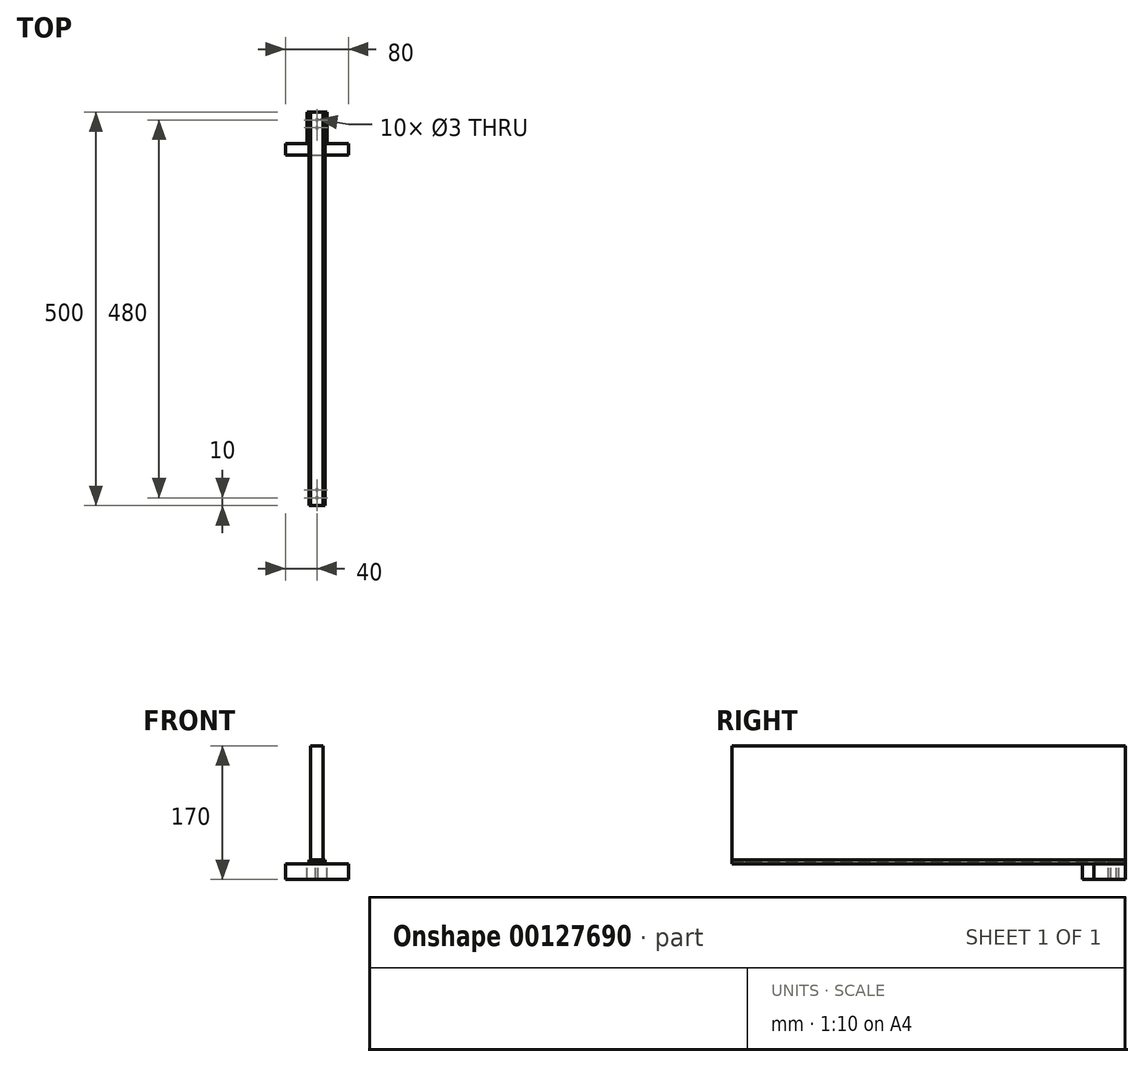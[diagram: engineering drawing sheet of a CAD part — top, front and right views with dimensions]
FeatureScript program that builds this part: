
annotation { "Feature Type Name" : "Feature", "Feature Type Description" : "" }
export const myFeature = defineFeature(function(context is Context, id is Id, definition is map)
    precondition{}
    {
        {
            var Q0;
            Q0=qCreatedBy(makeId("Front.planeOp"),FACE);
            var sketch = newSketch(context, id + "F0", { "sketchPlane" : qUnion([Q0])});
            skLineSegment(sketch, "E0", {"start": v(-8, 5) * mm, "end": v(-10, 5) * mm});
            skLineSegment(sketch, "E1", {"start": v(-10, 5) * mm, "end": v(-10, 0) * mm});
            skLineSegment(sketch, "E2", {"start": v(-10, 0) * mm, "end": v(0, 0) * mm});
            skLineSegment(sketch, "E3", {"start": v(0, 0) * mm, "end": v(0, 1) * mm});
            skLineSegment(sketch, "E4", {"start": v(0, 1) * mm, "end": v(-9, 1) * mm});
            skLineSegment(sketch, "E5", {"start": v(-9, 1) * mm, "end": v(-9, 4) * mm});
            skLineSegment(sketch, "E6", {"start": v(-9, 4) * mm, "end": v(-8, 4) * mm});
            skLineSegment(sketch, "E7", {"start": v(-8, 4) * mm, "end": v(-8, 5) * mm});
            skLineSegment(sketch, "E8.MirrorCS", {"start": v(8, 5) * mm, "end": v(10, 5) * mm});
            skLineSegment(sketch, "E9.MirrorCS", {"start": v(10, 5) * mm, "end": v(10, 0) * mm});
            skLineSegment(sketch, "E10.MirrorCS", {"start": v(8, 4) * mm, "end": v(8, 5) * mm});
            skLineSegment(sketch, "E11.MirrorCS", {"start": v(9, 4) * mm, "end": v(8, 4) * mm});
            skLineSegment(sketch, "E12.MirrorCS", {"start": v(9, 1) * mm, "end": v(9, 4) * mm});
            skLineSegment(sketch, "E13.MirrorCS", {"start": v(0, 1) * mm, "end": v(9, 1) * mm});
            skLineSegment(sketch, "E14.MirrorCS", {"start": v(10, 0) * mm, "end": v(0, 0) * mm});
            skSolve(sketch);
        }
        {
            var Q0;
            Q0 = qSketchRegion(id + "F0", true);
            extrude(context, id + "F1", {"entities" : qUnion([Q0]), "depth" : 500 * mm});
        }
        {
            var Q0;
            Q0=qCreatedBy(makeId("Front.planeOp"),FACE);
            var sketch = newSketch(context, id + "F2", { "sketchPlane" : qUnion([Q0])});
            skLineSegment(sketch, "E15", {"start": v(-7.9, 5) * mm, "end": v(-7.9, 3.9) * mm});
            skLineSegment(sketch, "E16", {"start": v(-7.9, 3.9) * mm, "end": v(-8.9, 3.9) * mm});
            skLineSegment(sketch, "E17", {"start": v(-8.9, 3.9) * mm, "end": v(-8.9, 1.1) * mm});
            skLineSegment(sketch, "E18", {"start": v(-8.9, 1.1) * mm, "end": v(0, 1.1) * mm});
            skLineSegment(sketch, "E19", {"start": v(-7.9, 5) * mm, "end": v(0, 5) * mm});
            skLineSegment(sketch, "E20", {"start": v(0, 5) * mm, "end": v(0, 1.1) * mm});
            skLineSegment(sketch, "E21.MirrorCS", {"start": v(7.9, 5) * mm, "end": v(0, 5) * mm});
            skLineSegment(sketch, "E22.MirrorCS", {"start": v(7.9, 5) * mm, "end": v(7.9, 3.9) * mm});
            skLineSegment(sketch, "E23.MirrorCS", {"start": v(7.9, 3.9) * mm, "end": v(8.9, 3.9) * mm});
            skLineSegment(sketch, "E24.MirrorCS", {"start": v(8.9, 3.9) * mm, "end": v(8.9, 1.1) * mm});
            skLineSegment(sketch, "E25.MirrorCS", {"start": v(8.9, 1.1) * mm, "end": v(0, 1.1) * mm});
            skSolve(sketch);
        }
        {
            var Q0;
            Q0 = qSketchRegion(id + "F2", true);
            extrude(context, id + "F3", {"entities" : qUnion([Q0]), "depth" : 500 * mm});
        }
        {
            var Q0;
            Q0=makeQuery(id+"F3.opExtrude","SWEPT_FACE",FACE,{"disambiguationData":[OSD([sQuery(id+"F2.wireOp",EDGE,"E19"),sQuery(id+"F2.wireOp",EDGE,"E21.MirrorCS")])]});
            var sketch = newSketch(context, id + "F4", { "sketchPlane" : qUnion([Q0])});
            skCircle(sketch, "E26", {"center": v(0, -10) * mm, "radius": 1.5 * mm});
            skCircle(sketch, "E27", {"center": v(0, -490) * mm, "radius": 1.5 * mm});
            skCircle(sketch, "E28", {"center": v(0, -20) * mm, "radius": 1.5 * mm});
            skCircle(sketch, "E29", {"center": v(0, -480) * mm, "radius": 1.5 * mm});
            skSolve(sketch);
        }
        {
            var Q0;
            Q0=makeQuery(id+"F4.imprint","IMPRINT",FACE,{"disambiguationData":[TD([[makeQuery(id+"F4.imprint","IMPRINT",EDGE,{"derivedFrom":sQuery(id+"F4.wireOp",EDGE,"E27")}),1.0]])]});
            var Q1;
            Q1=makeQuery(id+"F4.imprint","IMPRINT",FACE,{"disambiguationData":[TD([[makeQuery(id+"F4.imprint","IMPRINT",EDGE,{"derivedFrom":sQuery(id+"F4.wireOp",EDGE,"E29")}),1.0]])]});
            var Q2;
            Q2=makeQuery(id+"F4.imprint","IMPRINT",FACE,{"disambiguationData":[TD([[makeQuery(id+"F4.imprint","IMPRINT",EDGE,{"derivedFrom":sQuery(id+"F4.wireOp",EDGE,"E28")}),1.0]])]});
            var Q3;
            Q3=makeQuery(id+"F4.imprint","IMPRINT",FACE,{"disambiguationData":[TD([[makeQuery(id+"F4.imprint","IMPRINT",EDGE,{"derivedFrom":sQuery(id+"F4.wireOp",EDGE,"E26")}),1.0]])]});
            var Q4;
            Q4=sQuery(id+"F4.wireOp",EDGE,"E27");
            extrude(context, id + "F5", {"entities" : qUnion([Q0, Q1, Q2, Q3]), "surfaceEntities" : qUnion([Q4]), "endBound" : BoundingType.SYMMETRIC, "oppositeDirection" : true, "depth" : 15 * mm});
        }
        {
            var Q0;
            Q0=makeQuery(id+"F5.opExtrude","SWEPT_BODY",BODY,{"disambiguationData":[OSD([sQuery(id+"F4.wireOp",EDGE,"E26")])]});
            var Q1;
            Q1=makeQuery(id+"F5.opExtrude","SWEPT_BODY",BODY,{"disambiguationData":[OSD([sQuery(id+"F4.wireOp",EDGE,"E28")])]});
            var Q2;
            Q2=makeQuery(id+"F5.opExtrude","SWEPT_BODY",BODY,{"disambiguationData":[OSD([sQuery(id+"F4.wireOp",EDGE,"E29")])]});
            var Q3;
            Q3=makeQuery(id+"F5.opExtrude","SWEPT_BODY",BODY,{"disambiguationData":[OSD([sQuery(id+"F4.wireOp",EDGE,"E27")])]});
            var Q4;
            Q4=makeQuery(id+"F3.opExtrude","SWEPT_BODY",BODY,{"disambiguationData":[OSD([sQuery(id+"F2.wireOp",EDGE,"E15"),sQuery(id+"F2.wireOp",EDGE,"E17"),sQuery(id+"F2.wireOp",EDGE,"E18"),sQuery(id+"F2.wireOp",EDGE,"E19"),sQuery(id+"F2.wireOp",EDGE,"E16"),sQuery(id+"F2.wireOp",EDGE,"E21.MirrorCS"),sQuery(id+"F2.wireOp",EDGE,"E22.MirrorCS"),sQuery(id+"F2.wireOp",EDGE,"E23.MirrorCS"),sQuery(id+"F2.wireOp",EDGE,"E24.MirrorCS"),sQuery(id+"F2.wireOp",EDGE,"E25.MirrorCS")])]});
            var Q5;
            Q5=makeQuery(id+"F1.opExtrude","SWEPT_BODY",BODY,{"disambiguationData":[OSD([sQuery(id+"F0.wireOp",EDGE,"E0"),sQuery(id+"F0.wireOp",EDGE,"E1"),sQuery(id+"F0.wireOp",EDGE,"E2"),sQuery(id+"F0.wireOp",EDGE,"E4"),sQuery(id+"F0.wireOp",EDGE,"E5"),sQuery(id+"F0.wireOp",EDGE,"E6"),sQuery(id+"F0.wireOp",EDGE,"E7"),sQuery(id+"F0.wireOp",EDGE,"E8.MirrorCS"),sQuery(id+"F0.wireOp",EDGE,"E9.MirrorCS"),sQuery(id+"F0.wireOp",EDGE,"E10.MirrorCS"),sQuery(id+"F0.wireOp",EDGE,"E11.MirrorCS"),sQuery(id+"F0.wireOp",EDGE,"E12.MirrorCS"),sQuery(id+"F0.wireOp",EDGE,"E13.MirrorCS"),sQuery(id+"F0.wireOp",EDGE,"E14.MirrorCS")])]});
            booleanBodies(context, id + "F6", {"operationType" : BooleanOperationType.SUBTRACTION, "tools" : qUnion([Q0, Q1, Q2, Q3]), "targets" : qUnion([Q4, Q5])});
        }
        {
            var Q0;
            Q0=qCreatedBy(makeId("Top.planeOp"),FACE);
            var sketch = newSketch(context, id + "F7", { "sketchPlane" : qUnion([Q0])});
            skLineSegment(sketch, "E30.bottom", {"start": v(-8, 0) * mm, "end": v(8, 0) * mm});
            skLineSegment(sketch, "E30.top", {"start": v(-8, -500) * mm, "end": v(8, -500) * mm});
            skLineSegment(sketch, "E30.left", {"start": v(-8, 0) * mm, "end": v(-8, -500) * mm});
            skLineSegment(sketch, "E30.right", {"start": v(8, 0) * mm, "end": v(8, -500) * mm});
            skSolve(sketch);
        }
        {
            var Q0;
            Q0 = qSketchRegion(id + "F7", true);
            extrude(context, id + "F8", {"entities" : qUnion([Q0]), "depth" : 150 * mm});
        }
        {
            var Q0;
            Q0=qCreatedBy(makeId("Top.planeOp"),FACE);
            var sketch = newSketch(context, id + "F9", { "sketchPlane" : qUnion([Q0])});
            skLineSegment(sketch, "E31", {"start": v(40, -40) * mm, "end": v(12.5, -40) * mm});
            skLineSegment(sketch, "E32", {"start": v(12.5, -40) * mm, "end": v(12.5, 0) * mm});
            skLineSegment(sketch, "E33", {"start": v(12.5, 0) * mm, "end": v(-12.5, 0) * mm});
            skLineSegment(sketch, "E34", {"start": v(-12.5, 0) * mm, "end": v(-12.5, -40) * mm});
            skLineSegment(sketch, "E35", {"start": v(-12.5, -40) * mm, "end": v(-40, -40) * mm});
            skLineSegment(sketch, "E36", {"start": v(-40, -40) * mm, "end": v(-40, -55) * mm});
            skLineSegment(sketch, "E37", {"start": v(-40, -55) * mm, "end": v(40, -55) * mm});
            skLineSegment(sketch, "E38", {"start": v(40, -55) * mm, "end": v(40, -40) * mm});
            skCircle(sketch, "E39", {"center": v(0, -10) * mm, "radius": 1.5 * mm});
            skCircle(sketch, "E40", {"center": v(0, -20) * mm, "radius": 1.5 * mm});
            skSolve(sketch);
        }
        {
            var Q0;
            Q0 = qSketchRegion(id + "F9", true);
            extrude(context, id + "F10", {"entities" : qUnion([Q0]), "oppositeDirection" : true, "depth" : 20 * mm});
        }
    });
